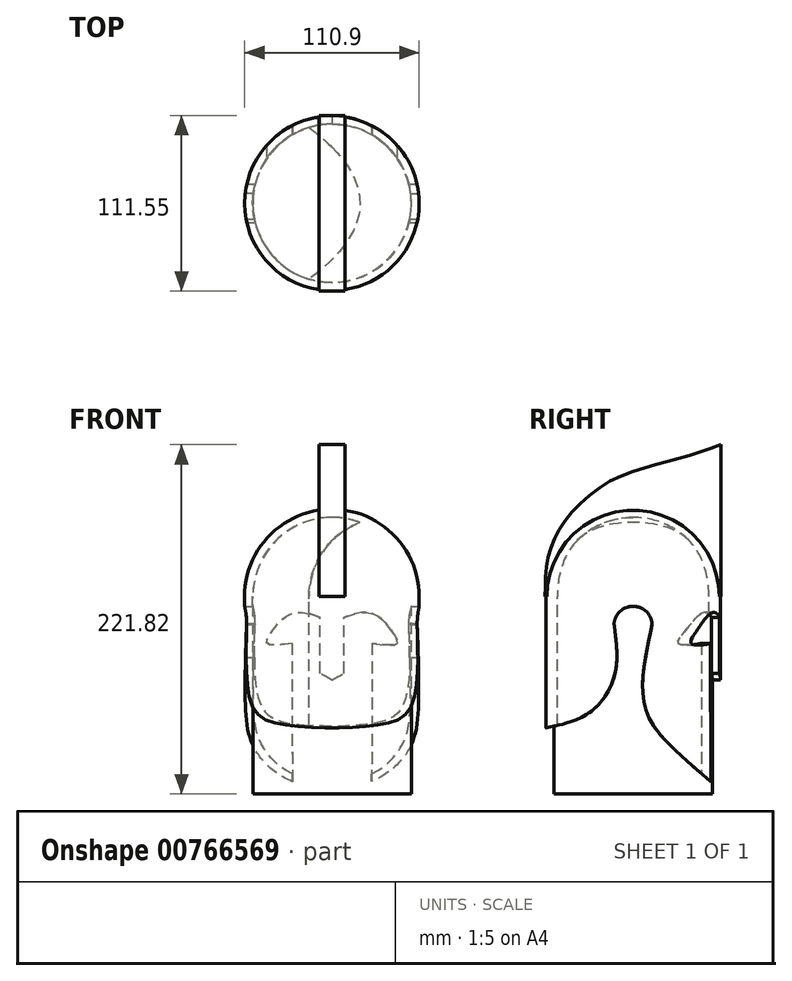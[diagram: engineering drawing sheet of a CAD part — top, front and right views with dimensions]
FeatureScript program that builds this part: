
annotation { "Feature Type Name" : "Feature", "Feature Type Description" : "" }
export const myFeature = defineFeature(function(context is Context, id is Id, definition is map)
    precondition{}
    {
        {
            var Q0;
            Q0=qCreatedBy(makeId("Front.planeOp"),FACE);
            var sketch = newSketch(context, id + "F0", { "sketchPlane" : qUnion([Q0])});
            skPoint(sketch, "E0.1.internal.orphan", {"position": v(21.55, 61.03) * mm});
            skPoint(sketch, "E1.end.orphan", {"position": v(0, 31.5) * mm});
            skPoint(sketch, "E1.start.orphan", {"position": v(0, 61.03) * mm});
            skLineSegment(sketch, "E2", {"start": v(55.52, 0) * mm, "end": v(55.52, 0) * mm});
            skLineSegment(sketch, "E3", {"start": v(-55.52, 0) * mm, "end": v(-55.52, -139.9) * mm});
            skLineSegment(sketch, "E4", {"start": v(-55.52, -139.9) * mm, "end": v(-50.37, -139.9) * mm});
            skLineSegment(sketch, "E5", {"start": v(-0.07, 55.52) * mm, "end": v(-0.07, -139.9) * mm});
            skPoint(sketch, "E5.startSnap0", {"position": v(0.07, 55.52) * mm});
            skArc(sketch, "E6.trimOffspring", {"start": v(0.07, 55.52) * mm, "mid": v(-39.23, 39.28) * mm, "end": v(-55.52, 0) * mm});
            skArc(sketch, "E7", {"start": v(-0.07, 50.37) * mm, "mid": v(-35.64, 35.59) * mm, "end": v(-50.37, 0) * mm});
            skLineSegment(sketch, "E8", {"start": v(-50.37, 0) * mm, "end": v(-50.37, -139.9) * mm});
            skSolve(sketch);
        }
        {
            var Q0;
            {var subQ0=sQuery(id+"F0.wireOp",EDGE,"E3");Q0=makeQuery(id+"F0.imprint","IMPRINT",FACE,{"disambiguationData":[TD([[makeQuery(id+"F0.imprint","IMPRINT",EDGE,{"derivedFrom":subQ0}),1.0]])]});}
            var Q1;
            Q1=sQuery(id+"F0.wireOp",EDGE,"E5");
            revolve(context, id + "F1", {"surfaceOperationType" : NewSurfaceOperationType.NEW, "entities" : qUnion([Q0]), "axis" : qUnion([Q1]), "revolveType" : RevolveType.FULL});
        }
        {
            var Q0;
            Q0=qCreatedBy(makeId("Front.planeOp"),FACE);
            var sketch = newSketch(context, id + "F2", { "sketchPlane" : qUnion([Q0])});
            skLineSegment(sketch, "E9", {"start": v(0, -53) * mm, "end": v(-7.54, -48.77) * mm});
            skLineSegment(sketch, "E10", {"start": v(-7.54, -48.77) * mm, "end": v(-7.54, -13.31) * mm});
            skLineSegment(sketch, "E11", {"start": v(-25.44, -29.69) * mm, "end": v(-25.15, -139.45) * mm});
            skPoint(sketch, "E12.2.internal.orphan", {"position": v(-23.22, -9.18) * mm});
            skPoint(sketch, "E12.3.internal.orphan", {"position": v(-35.9, -13.31) * mm});
            skFitSpline(sketch, "E13", {"points": [v(-7.54, -13.31) * mm, v(-17.19, -10.39) * mm, v(-28.22, -11.94) * mm, v(-38.73, -22.97) * mm, v(-41.31, -29.69) * mm, v(-25.44, -29.69) * mm], "startDerivative": vector(-50.3, 19.36) * mm, "endDerivative": vector(92.69, 12.31) * mm});
            skLineSegment(sketch, "E14.MirrorCS", {"start": v(0, -53) * mm, "end": v(7.54, -48.77) * mm});
            skLineSegment(sketch, "E15.MirrorCS", {"start": v(7.54, -48.77) * mm, "end": v(7.54, -13.31) * mm});
            skFitSpline(sketch, "E16.MirrorCS", {"points": [v(7.54, -13.31) * mm, v(17.19, -10.39) * mm, v(28.22, -11.94) * mm, v(38.73, -22.97) * mm, v(41.31, -29.69) * mm, v(25.44, -29.69) * mm], "startDerivative": vector(50.3, 19.36) * mm, "endDerivative": vector(-92.69, 12.31) * mm});
            skLineSegment(sketch, "E17.MirrorCS", {"start": v(25.44, -29.69) * mm, "end": v(25.15, -139.32) * mm});
            skPoint(sketch, "E18.orphan", {"position": v(23.22, -864.35) * mm});
            skPoint(sketch, "E19.orphan", {"position": v(-23.22, -864.35) * mm});
            skLineSegment(sketch, "E20", {"start": v(25.15, -139.32) * mm, "end": v(25.17, -147.8) * mm});
            skLineSegment(sketch, "E21", {"start": v(25.17, -147.8) * mm, "end": v(-25.15, -147.94) * mm});
            skLineSegment(sketch, "E22", {"start": v(-25.15, -147.94) * mm, "end": v(-25.15, -139.45) * mm});
            skSolve(sketch);
        }
        {
            var Q0;
            Q0 = qSketchRegion(id + "F2", true);
            extrude(context, id + "F3", {"entities" : qUnion([Q0]), "operationType" : NewBodyOperationType.REMOVE, "oppositeDirection" : true, "depth" : 78.23 * mm, "offsetDistance" : 25.4 * mm});
        }
        {
            var Q0;
            Q0=qCreatedBy(makeId("Right.planeOp"),FACE);
            var sketch = newSketch(context, id + "F4", { "sketchPlane" : qUnion([Q0])});
            skArc(sketch, "E23", {"start": v(12.12, -17.77) * mm, "mid": v(0.29, -6.13) * mm, "end": v(-12.08, -17.2) * mm});
            skFitSpline(sketch, "E24", {"points": [v(12.12, -17.77) * mm, v(7.46, -69.7) * mm, v(26.09, -96.83) * mm, v(49.54, -117.65) * mm], "startDerivative": vector(-31.96, -145.55) * mm, "endDerivative": vector(78.13, -66.73) * mm});
            skFitSpline(sketch, "E25", {"points": [v(-12.08, -17.2) * mm, v(-10.28, -35.18) * mm, v(-10, -66.24) * mm], "startDerivative": vector(4.98, -38.7) * mm, "endDerivative": vector(-0.57, -58.5) * mm});
            skLineSegment(sketch, "E26", {"start": v(49.54, -117.65) * mm, "end": v(49.54, -138.86) * mm});
            skLineSegment(sketch, "E27", {"start": v(49.54, -138.86) * mm, "end": v(49.54, -146.64) * mm});
            skLineSegment(sketch, "E28", {"start": v(49.54, -146.64) * mm, "end": v(-55.95, -146.64) * mm});
            skLineSegment(sketch, "E29", {"start": v(-55.95, -146.64) * mm, "end": v(-55.95, -83.45) * mm});
            skFitSpline(sketch, "E30", {"points": [v(-55.95, -83.45) * mm, v(-32.62, -76.65) * mm, v(-16.74, -61.74) * mm, v(-10.26, -41.33) * mm, v(-11.37, -22.78) * mm], "startDerivative": vector(92.34, 18.05) * mm, "endDerivative": vector(-10.57, 78.25) * mm});
            skLineSegment(sketch, "E31", {"start": v(-11.37, -22.78) * mm, "end": v(-11.44, -22.29) * mm});
            skSolve(sketch);
        }
        {
            var Q0;
            Q0 = qSketchRegion(id + "F4", true);
            extrude(context, id + "F5", {"entities" : qUnion([Q0]), "operationType" : NewBodyOperationType.REMOVE, "endBound" : BoundingType.SYMMETRIC, "oppositeDirection" : true, "depth" : 153.42 * mm, "offsetDistance" : 25.4 * mm});
        }
        {
            var Q0;
            Q0=qCreatedBy(makeId("Right.planeOp"),FACE);
            var sketch = newSketch(context, id + "F6", { "sketchPlane" : qUnion([Q0])});
            skLineSegment(sketch, "E32", {"start": v(55.73, 0) * mm, "end": v(55.73, 96.5) * mm});
            skFitSpline(sketch, "E33", {"points": [v(-55.82, 0) * mm, v(-53.8, 25.4) * mm, v(-42.03, 49.72) * mm, v(-12.19, 74.54) * mm, v(24.17, 86.33) * mm, v(55.73, 96.5) * mm], "startDerivative": vector(1.37, 145.37) * mm, "endDerivative": vector(151.83, 52.9) * mm});
            skLineSegment(sketch, "E34", {"start": v(-55.82, 0) * mm, "end": v(-51.3, 0) * mm});
            skArc(sketch, "E35", {"start": v(51.3, 0) * mm, "mid": v(0, 51.3) * mm, "end": v(-51.3, 0) * mm});
            skLineSegment(sketch, "E36", {"start": v(55.73, 0) * mm, "end": v(51.3, 0) * mm});
            skSolve(sketch);
        }
        {
            var Q0;
            Q0=makeQuery(id+"F6.imprint","IMPRINT",FACE,{"disambiguationData":[TD([[makeQuery(id+"F6.imprint","IMPRINT",EDGE,{"derivedFrom":sQuery(id+"F6.wireOp",EDGE,"E32")}),1.0]])]});
            extrude(context, id + "F7", {"entities" : qUnion([Q0]), "operationType" : NewBodyOperationType.ADD, "endBound" : BoundingType.SYMMETRIC, "depth" : 16.76 * mm, "offsetDistance" : 25.4 * mm});
        }
        {
            var Q0;
            Q0=qCreatedBy(makeId("Right.planeOp"),FACE);
            var sketch = newSketch(context, id + "F8", { "sketchPlane" : qUnion([Q0])});
            skLineSegment(sketch, "E37", {"start": v(0, 50.36) * mm, "end": v(0, -123.94) * mm});
            skLineSegment(sketch, "E38", {"start": v(-50.32, 0) * mm, "end": v(-50.32, -125.33) * mm});
            skLineSegment(sketch, "E39", {"start": v(-50.32, -125.33) * mm, "end": v(0, -125.33) * mm});
            skLineSegment(sketch, "E40", {"start": v(0, -125.33) * mm, "end": v(0, -123.94) * mm});
            skArc(sketch, "E41", {"start": v(0, 50.32) * mm, "mid": v(-35.58, 35.58) * mm, "end": v(-50.32, 0) * mm});
            skSolve(sketch);
        }
        {
            var Q0;
            Q0=makeQuery(id+"F8.imprint","IMPRINT",FACE,{"disambiguationData":[TD([[makeQuery(id+"F8.imprint","IMPRINT",EDGE,{"derivedFrom":sQuery(id+"F8.wireOp",EDGE,"E38")}),1.0]])]});
            var Q1;
            Q1=sQuery(id+"F8.wireOp",EDGE,"E37");
            revolve(context, id + "F9", {"operationType" : NewBodyOperationType.ADD, "surfaceOperationType" : NewSurfaceOperationType.NEW, "entities" : qUnion([Q0]), "axis" : qUnion([Q1]), "revolveType" : RevolveType.FULL});
        }
    });
